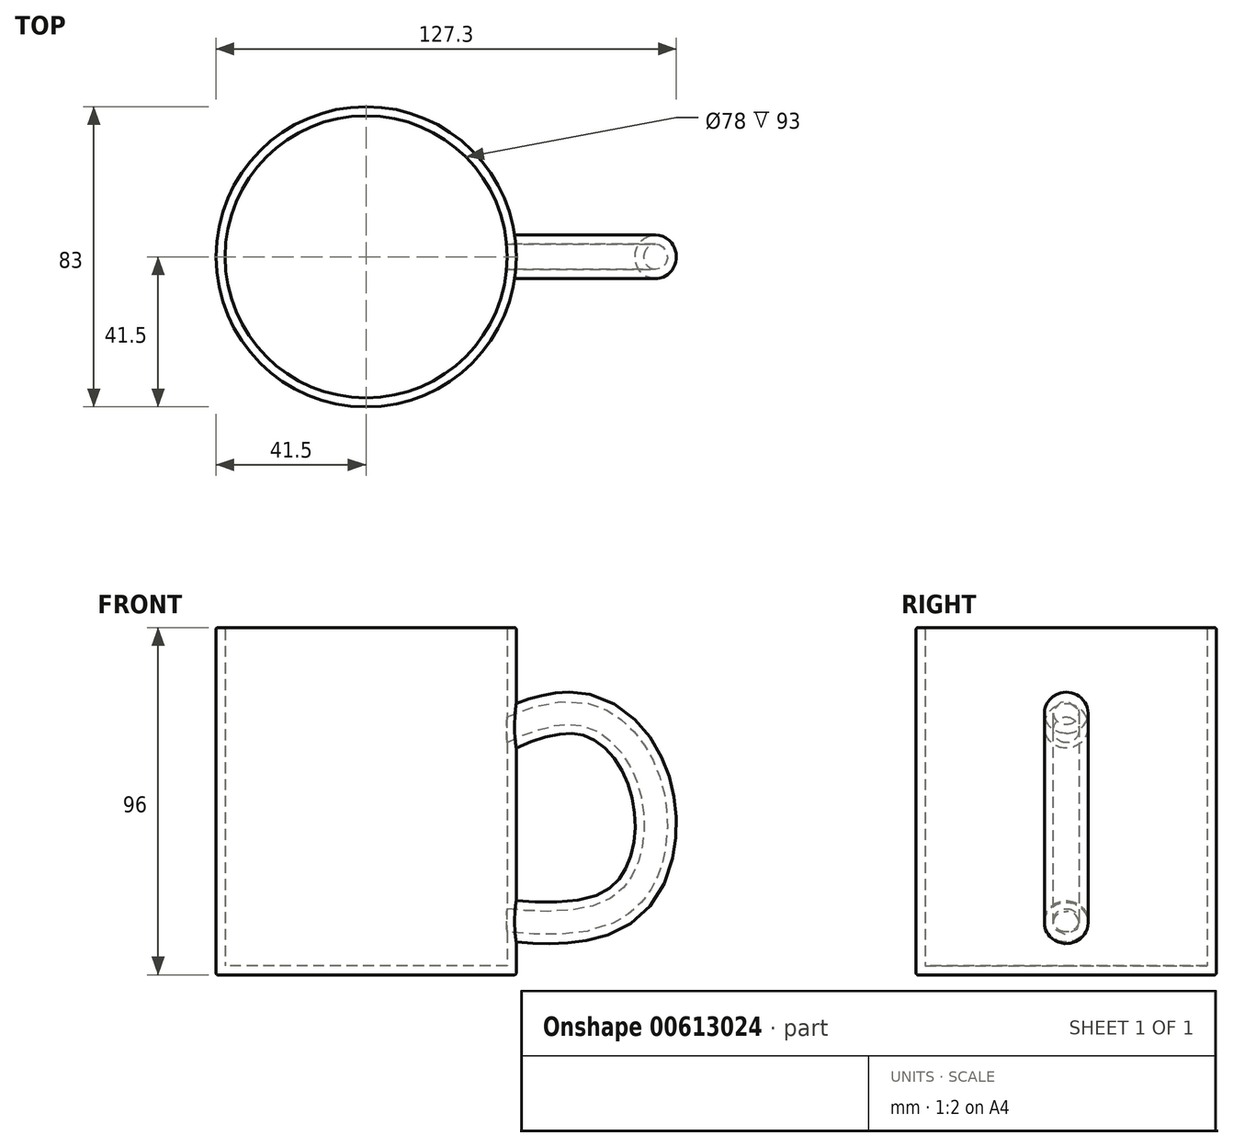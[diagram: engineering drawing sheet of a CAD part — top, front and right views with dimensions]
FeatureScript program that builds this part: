
annotation { "Feature Type Name" : "Feature", "Feature Type Description" : "" }
export const myFeature = defineFeature(function(context is Context, id is Id, definition is map)
    precondition{}
    {
        {
            var Q0;
            Q0=qCreatedBy(makeId("Top.planeOp"),FACE);
            var sketch = newSketch(context, id + "F0", { "sketchPlane" : qUnion([Q0])});
            skCircle(sketch, "E0", {"center": v(0, 0) * mm, "radius": 41.5 * mm});
            skSolve(sketch);
        }
        {
            var Q0;
            Q0 = qSketchRegion(id + "F0", true);
            extrude(context, id + "F1", {"entities" : qUnion([Q0]), "depth" : 96 * mm, "offsetDistance" : 25 * mm});
        }
        {
            var Q0;
            Q0=qCreatedBy(makeId("Front.planeOp"),FACE);
            var sketch = newSketch(context, id + "F2", { "sketchPlane" : qUnion([Q0])});
            skFitSpline(sketch, "E1", {"points": [v(37.24, 65.63) * mm, v(59.61, 70.96) * mm, v(75.32, 57.59) * mm, v(78.18, 34.19) * mm, v(63.6, 17.15) * mm, v(32.99, 17.59) * mm, v(32.99, 18.1) * mm], "startDerivative": vector(100.58, 52.92) * mm, "endDerivative": vector(62.12, 13.61) * mm});
            skSolve(sketch);
        }
        {
            var Q0;
            Q0=qCreatedBy(makeId("Right.planeOp"),FACE);
            cPlane(context, id + "F3", {"entities" : qUnion([Q0]), "cplaneType" : CPlaneType.OFFSET, "offset" : 45 * mm, "width" : 150 * mm, "height" : 150 * mm});
        }
        {
            var Q0;
            Q0=qCreatedBy(id+"F3.planeOp",FACE);
            var sketch = newSketch(context, id + "F4", { "sketchPlane" : qUnion([Q0])});
            skCircle(sketch, "E2", {"center": v(0, 70.23) * mm, "radius": 6.04 * mm});
            skSolve(sketch);
        }
        {
            var Q0;
            Q0=makeQuery(id+"F4.imprint","IMPRINT",FACE,{"disambiguationData":[TD([[makeQuery(id+"F4.imprint","IMPRINT",EDGE,{"derivedFrom":sQuery(id+"F4.wireOp",EDGE,"E2")}),1.0]])]});
            var Q1;
            Q1=sQuery(id+"F4.wireOp",EDGE,"E2");
            var Q2;
            Q2=sQuery(id+"F2.wireOp",EDGE,"E1");
            sweep(context, id + "F5", {"operationType" : NewBodyOperationType.ADD, "profiles" : qUnion([Q0]), "surfaceProfiles" : qUnion([Q1]), "path" : qUnion([Q2])});
        }
        {
            var Q0;
            Q0=makeQuery(id+"F1.opExtrude","CAP_FACE",FACE,{"disambiguationData":[OSD([sQuery(id+"F0.wireOp",EDGE,"E0")])],"isStart":false});
            shell(context, id + "F6", {"entities" : qUnion([Q0]), "thickness" : 2.5 * mm});
        }
        {
            var Q0;
            {var subQ0=sQuery(id+"F0.wireOp",EDGE,"E0");Q0=makeQuery(id+"F6.opShell","OFFSET_EDGE",EDGE,{"disambiguationData":[OSD([subQ0]),TDD([makeQuery(id+"F1.opExtrude","CAP_EDGE",EDGE,{"disambiguationData":[OSD([subQ0])],"isStart":false})])]});}
            var Q1;
            Q1=makeQuery(id+"F1.opExtrude","CAP_EDGE",EDGE,{"disambiguationData":[OSD([sQuery(id+"F0.wireOp",EDGE,"E0")])],"isStart":false});
            fillet(context, id + "F7", {"entities" : qUnion([Q0, Q1]), "radius" : 0.5 * mm, "tangentPropagation" : true, "allowEdgeOverflow" : false});
        }
        {
            var Q0;
            Q0=makeQuery(id+"F1.opExtrude","CAP_EDGE",EDGE,{"disambiguationData":[OSD([sQuery(id+"F0.wireOp",EDGE,"E0")])],"isStart":true});
            fillet(context, id + "F8", {"entities" : qUnion([Q0]), "radius" : 0.5 * mm, "tangentPropagation" : true, "allowEdgeOverflow" : false});
        }
    });
